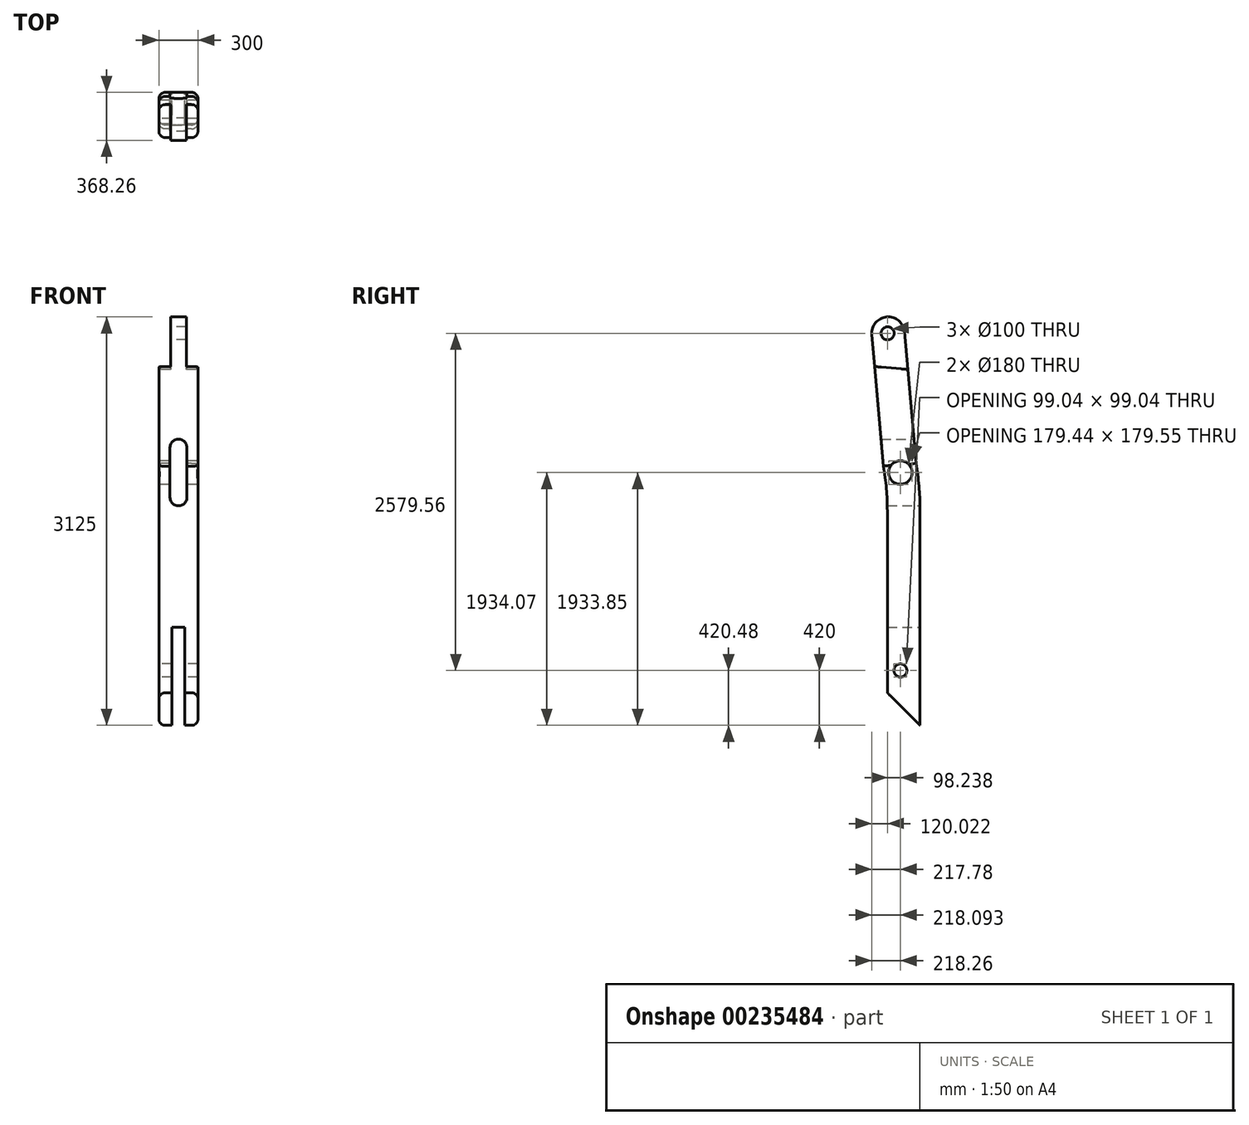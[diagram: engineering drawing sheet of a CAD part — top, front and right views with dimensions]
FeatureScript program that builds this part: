
annotation { "Feature Type Name" : "Feature", "Feature Type Description" : "" }
export const myFeature = defineFeature(function(context is Context, id is Id, definition is map)
    precondition{}
    {
        {
            var Q0;
            Q0=qCreatedBy(makeId("Right.planeOp"),FACE);
            var sketch = newSketch(context, id + "F0", { "sketchPlane" : qUnion([Q0])});
            skLineSegment(sketch, "E0", {"start": v(0, 0) * mm, "end": v(0, 1655.63) * mm});
            skLineSegment(sketch, "E1", {"start": v(-250, 250) * mm, "end": v(-250, 1639.25) * mm});
            skLineSegment(sketch, "E2", {"start": v(-30.7, 2004.74) * mm, "end": v(-118.73, 3010.9) * mm});
            skLineSegment(sketch, "E3", {"start": v(-279.75, 1982.95) * mm, "end": v(-367.78, 2989.1) * mm});
            skLineSegment(sketch, "E4", {"start": v(0, 0) * mm, "end": v(-250, 250) * mm});
            skArc(sketch, "E5", {"start": v(-118.73, 3010.9) * mm, "mid": v(-254.15, 3124.52) * mm, "end": v(-367.78, 2989.1) * mm});
            skCircle(sketch, "E6", {"center": v(-150, 420) * mm, "radius": 50 * mm});
            skCircle(sketch, "E7", {"center": v(-248.24, 2999.56) * mm, "radius": 50 * mm});
            skLineSegment(sketch, "E8", {"start": v(-346.42, 2745) * mm, "end": v(-93.53, 2722.87) * mm});
            skLineSegment(sketch, "E9", {"start": v(-367.78, 2989.1) * mm, "end": v(-118.73, 3010.9) * mm, "construction": true});
            skPoint(sketch, "E10", {"position": v(-243.26, 3125) * mm});
            skCircle(sketch, "E11", {"center": v(-150, 1934.07) * mm, "radius": 90 * mm});
            skLineSegment(sketch, "E12", {"start": v(-125, -169.65) * mm, "end": v(-125, 1648.32) * mm, "construction": true});
            skLineSegment(sketch, "E13", {"start": v(-125, 1648.32) * mm, "end": v(-295.38, 3595.72) * mm, "construction": true});
            skArc(sketch, "E14", {"start": v(0, 1655.63) * mm, "mid": v(-7.7, 1830.86) * mm, "end": v(-30.7, 2004.74) * mm});
            skArc(sketch, "E15", {"start": v(-250, 1639.25) * mm, "mid": v(-257.45, 1811.74) * mm, "end": v(-279.75, 1982.95) * mm});
            skSolve(sketch);
        }
        {
            var Q0;
            Q0=makeQuery(id+"F0.imprint","IMPRINT",FACE,{"disambiguationData":[TD([[makeQuery(id+"F0.imprint","IMPRINT",EDGE,{"derivedFrom":sQuery(id+"F0.wireOp",EDGE,"E0")}),1.0]])]});
            extrude(context, id + "F1", {"entities" : qUnion([Q0]), "endBound" : BoundingType.SYMMETRIC, "depth" : 300 * mm});
        }
        {
            var Q0;
            {var subQ0=sQuery(id+"F0.wireOp",EDGE,"E5");Q0=makeQuery(id+"F0.imprint","IMPRINT",FACE,{"disambiguationData":[TD([[makeQuery(id+"F0.imprint","IMPRINT",EDGE,{"derivedFrom":subQ0}),1.0]])]});}
            extrude(context, id + "F2", {"entities" : qUnion([Q0]), "operationType" : NewBodyOperationType.ADD, "endBound" : BoundingType.SYMMETRIC, "depth" : 120 * mm});
        }
        {
            var Q0;
            Q0=qCreatedBy(makeId("Front.planeOp"),FACE);
            var sketch = newSketch(context, id + "F3", { "sketchPlane" : qUnion([Q0])});
            skLineSegment(sketch, "E16", {"start": v(-65, 2125) * mm, "end": v(-65, 1745) * mm});
            skLineSegment(sketch, "E17", {"start": v(65, 2125) * mm, "end": v(65, 1745) * mm});
            skArc(sketch, "E18", {"start": v(65, 1745) * mm, "mid": v(0, 1810) * mm, "end": v(-65, 1745) * mm, "construction": true});
            skArc(sketch, "E19", {"start": v(-65, 1745) * mm, "mid": v(0, 1680) * mm, "end": v(65, 1745) * mm});
            skArc(sketch, "E20", {"start": v(65, 2125) * mm, "mid": v(0, 2190) * mm, "end": v(-65, 2125) * mm});
            skArc(sketch, "E21", {"start": v(-65, 2125) * mm, "mid": v(0, 2060) * mm, "end": v(65, 2125) * mm, "construction": true});
            skLineSegment(sketch, "E22", {"start": v(-60, 3125) * mm, "end": v(60, 3125) * mm});
            skSolve(sketch);
        }
        {
            var Q0;
            Q0 = qSketchRegion(id + "F3", true);
            extrude(context, id + "F4", {"entities" : qUnion([Q0]), "operationType" : NewBodyOperationType.REMOVE, "depth" : 347 * mm});
        }
        {
            var Q0;
            Q0=makeQuery(id+"F1.opExtrude","SWEPT_FACE",FACE,{"disambiguationData":[OSD([sQuery(id+"F0.wireOp",EDGE,"E0")])]});
            var sketch = newSketch(context, id + "F5", { "sketchPlane" : qUnion([Q0])});
            skLineSegment(sketch, "E23.0", {"start": v(-150, 0) * mm, "end": v(150, 0) * mm});
            skLineSegment(sketch, "E24", {"start": v(-50, 0) * mm, "end": v(-50, 750) * mm});
            skLineSegment(sketch, "E25", {"start": v(-50, 750) * mm, "end": v(50, 750) * mm});
            skLineSegment(sketch, "E26.MirrorCS", {"start": v(50, 0) * mm, "end": v(50, 750) * mm});
            skSolve(sketch);
        }
        {
            var Q0;
            {var subQ0=sQuery(id+"F5.wireOp",EDGE,"E24");Q0=makeQuery(id+"F5.imprint","IMPRINT",FACE,{"disambiguationData":[TD([[makeQuery(id+"F5.imprint","IMPRINT",EDGE,{"derivedFrom":subQ0}),-1.0]])]});}
            extrude(context, id + "F6", {"entities" : qUnion([Q0]), "operationType" : NewBodyOperationType.REMOVE, "oppositeDirection" : true, "depth" : 340 * mm});
        }
        {
            var Q0;
            Q0=makeQuery(id+"F1.opExtrude","CAP_EDGE",EDGE,{"disambiguationData":[OSD([sQuery(id+"F0.wireOp",EDGE,"E3")])],"isStart":true});
            var Q1;
            Q1=makeQuery(id+"F1.opExtrude","CAP_EDGE",EDGE,{"disambiguationData":[OSD([sQuery(id+"F0.wireOp",EDGE,"E1")])],"isStart":true});
            var Q2;
            Q2=makeQuery(id+"F1.opExtrude","CAP_EDGE",EDGE,{"disambiguationData":[OSD([sQuery(id+"F0.wireOp",EDGE,"E15")])],"isStart":true});
            var Q3;
            Q3=makeQuery(id+"F1.opExtrude","CAP_EDGE",EDGE,{"disambiguationData":[OSD([sQuery(id+"F0.wireOp",EDGE,"E3")])],"isStart":false});
            var Q4;
            Q4=makeQuery(id+"F1.opExtrude","CAP_EDGE",EDGE,{"disambiguationData":[OSD([sQuery(id+"F0.wireOp",EDGE,"E15")])],"isStart":false});
            var Q5;
            Q5=makeQuery(id+"F1.opExtrude","CAP_EDGE",EDGE,{"disambiguationData":[OSD([sQuery(id+"F0.wireOp",EDGE,"E1")])],"isStart":false});
            var Q6;
            Q6=makeQuery(id+"F1.opExtrude","CAP_EDGE",EDGE,{"disambiguationData":[OSD([sQuery(id+"F0.wireOp",EDGE,"E0")])],"isStart":false});
            var Q7;
            Q7=makeQuery(id+"F1.opExtrude","CAP_EDGE",EDGE,{"disambiguationData":[OSD([sQuery(id+"F0.wireOp",EDGE,"E2")])],"isStart":false});
            var Q8;
            Q8=makeQuery(id+"F1.opExtrude","CAP_EDGE",EDGE,{"disambiguationData":[OSD([sQuery(id+"F0.wireOp",EDGE,"E14")])],"isStart":false});
            var Q9;
            Q9=makeQuery(id+"F1.opExtrude","CAP_EDGE",EDGE,{"disambiguationData":[OSD([sQuery(id+"F0.wireOp",EDGE,"E0")])],"isStart":true});
            var Q10;
            Q10=makeQuery(id+"F1.opExtrude","CAP_EDGE",EDGE,{"disambiguationData":[OSD([sQuery(id+"F0.wireOp",EDGE,"E14")])],"isStart":true});
            var Q11;
            Q11=makeQuery(id+"F1.opExtrude","CAP_EDGE",EDGE,{"disambiguationData":[OSD([sQuery(id+"F0.wireOp",EDGE,"E2")])],"isStart":true});
            fillet(context, id + "F7", {"entities" : qUnion([Q0, Q1, Q2, Q3, Q4, Q5, Q6, Q7, Q8, Q9, Q10, Q11]), "radius" : 50 * mm, "allowEdgeOverflow" : false});
        }
    });
